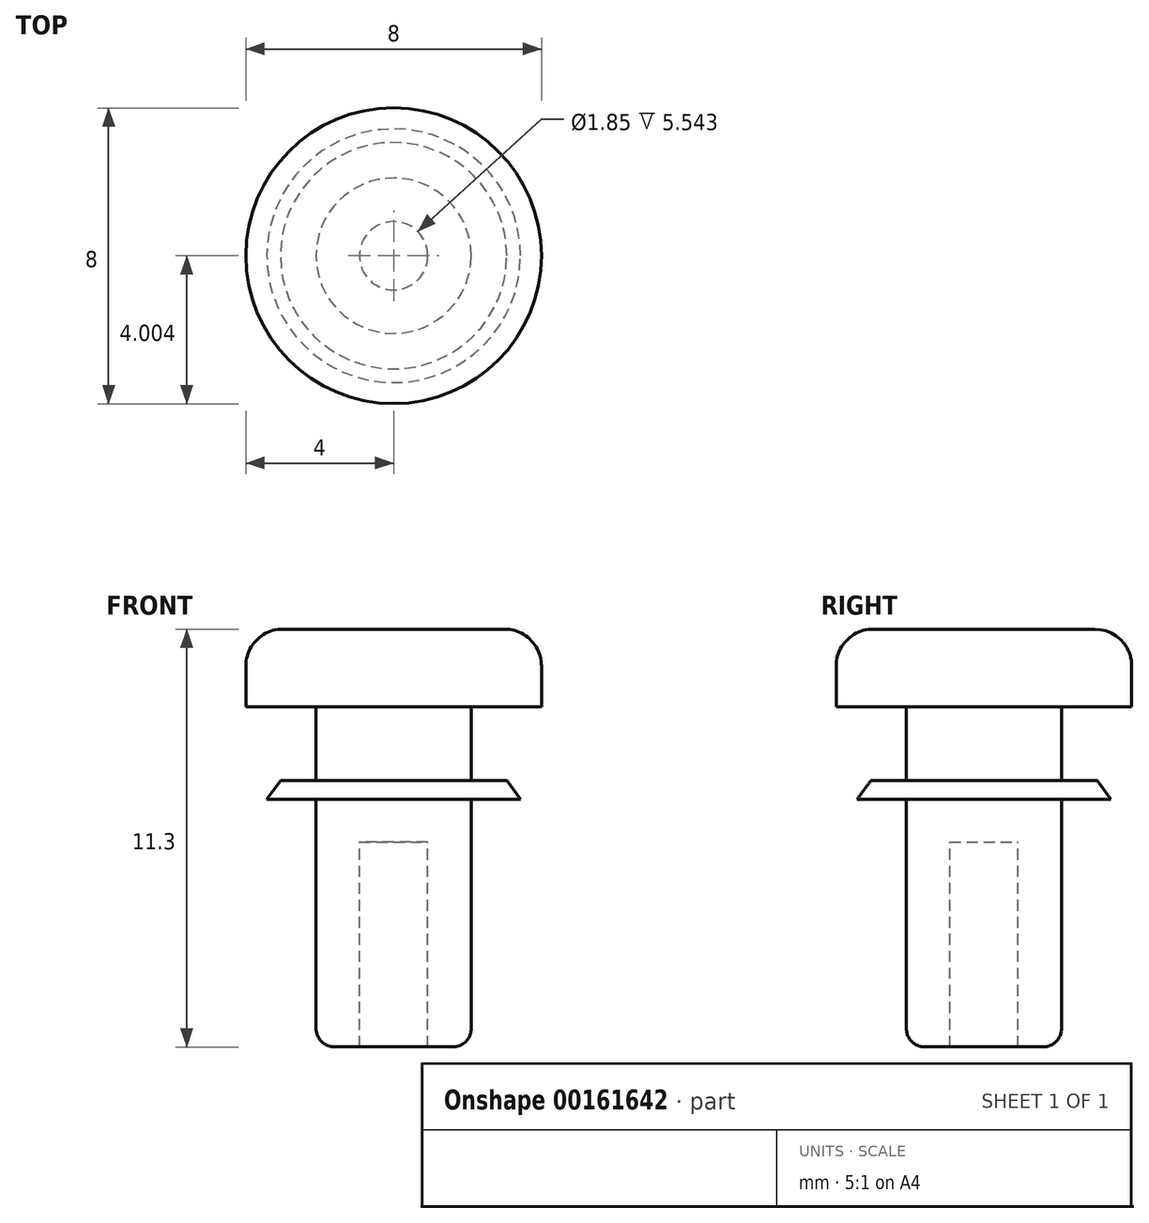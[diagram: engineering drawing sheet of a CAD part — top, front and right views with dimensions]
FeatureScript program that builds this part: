
annotation { "Feature Type Name" : "Feature", "Feature Type Description" : "" }
export const myFeature = defineFeature(function(context is Context, id is Id, definition is map)
    precondition{}
    {
        {
            var Q0;
            Q0=qCreatedBy(makeId("Right.planeOp"),FACE);
            var sketch = newSketch(context, id + "F0", { "sketchPlane" : qUnion([Q0])});
            skLineSegment(sketch, "E0", {"start": v(1.92, 4.52) * mm, "end": v(-1.08, 4.52) * mm});
            skLineSegment(sketch, "E1", {"start": v(-2.08, 3.52) * mm, "end": v(-2.08, 2.42) * mm});
            skLineSegment(sketch, "E2", {"start": v(-2.08, 2.42) * mm, "end": v(-0.18, 2.42) * mm});
            skLineSegment(sketch, "E3", {"start": v(-0.18, 2.42) * mm, "end": v(-0.18, 0.42) * mm});
            skLineSegment(sketch, "E4", {"start": v(-0.18, 0.42) * mm, "end": v(-1.14, 0.42) * mm});
            skLineSegment(sketch, "E5", {"start": v(-1.14, 0.42) * mm, "end": v(-1.5, -0.08) * mm});
            skLineSegment(sketch, "E6", {"start": v(-1.5, -0.08) * mm, "end": v(-0.18, -0.08) * mm});
            skLineSegment(sketch, "E7", {"start": v(-0.18, -0.08) * mm, "end": v(-0.18, -6.28) * mm});
            skLineSegment(sketch, "E8", {"start": v(0.32, -6.78) * mm, "end": v(1, -6.78) * mm});
            skPoint(sketch, "E9.visualSharp", {"position": v(-2.08, 4.52) * mm});
            skArc(sketch, "E9.filletArc", {"start": v(-1.08, 4.52) * mm, "mid": v(-1.78, 4.23) * mm, "end": v(-2.08, 3.52) * mm});
            skPoint(sketch, "E10.orphan", {"position": v(1.72, 2.42) * mm});
            skPoint(sketch, "E11.orphan", {"position": v(1.82, -0.08) * mm});
            skLineSegment(sketch, "E12", {"start": v(1.92, 4.52) * mm, "end": v(1.92, -1.23) * mm});
            skLineSegment(sketch, "E13", {"start": v(1, -6.78) * mm, "end": v(1, -1.23) * mm});
            skLineSegment(sketch, "E14", {"start": v(1, -1.23) * mm, "end": v(1.92, -1.23) * mm});
            skPoint(sketch, "E15.orphan", {"position": v(1.92, -6.78) * mm});
            skPoint(sketch, "E16.visualSharp", {"position": v(-0.18, -6.78) * mm});
            skArc(sketch, "E16.filletArc", {"start": v(-0.18, -6.28) * mm, "mid": v(-0.03, -6.63) * mm, "end": v(0.32, -6.78) * mm});
            skSolve(sketch);
        }
        {
            var Q0;
            Q0 = qSketchRegion(id + "F0", true);
            var Q1;
            Q1=sQuery(id+"F0.wireOp",EDGE,"E12");
            revolve(context, id + "F1", {"entities" : qUnion([Q0]), "axis" : qUnion([Q1]), "revolveType" : RevolveType.FULL});
        }
    });
